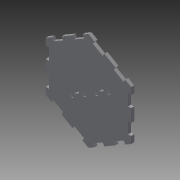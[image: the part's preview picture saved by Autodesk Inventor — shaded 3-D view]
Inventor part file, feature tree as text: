
AUTODESK INVENTOR PART (.ipt)
format: ipt  version: 2015 (Build 190159000, 159)  size: 186,880 bytes
history: native  units: mm
features: extrude x3, sketch x3
ambient origin geometry x8: Origin, YZ Plane, XZ Plane, XY Plane, X Axis, Y Axis, Z Axis, Center Point
bodies: Solid1 (feature_tree)
feature tree (6):
  extrude  "Extrusion1"  Depth=5.5mm
  extrude  "Extrusion2"  Depth=20.0mm
  extrude  "Extrusion3"  Depth=60.0mm TaperAngle=360.0deg
  sketch  "Sketch1"  dims[d4=150.0mm d6=86.60254mm d7=5.5mm]
  sketch  "Sketch2"  dims[d8=180.0deg d9=20.0mm]
  sketch  "Sketch4"  dims[d10=20.0mm d11=60.0mm d13=360.0deg d15=5.5mm d16=0.0mm d17=10.0mm d18=2.0mm d19=10.0mm d20=10.0mm d21=0.0mm d22=20.0mm d23=20.0mm d24=5.0mm d25=5.5mm d26=5.0mm d27=5.5mm d28=10.0mm d29=0.0mm]
